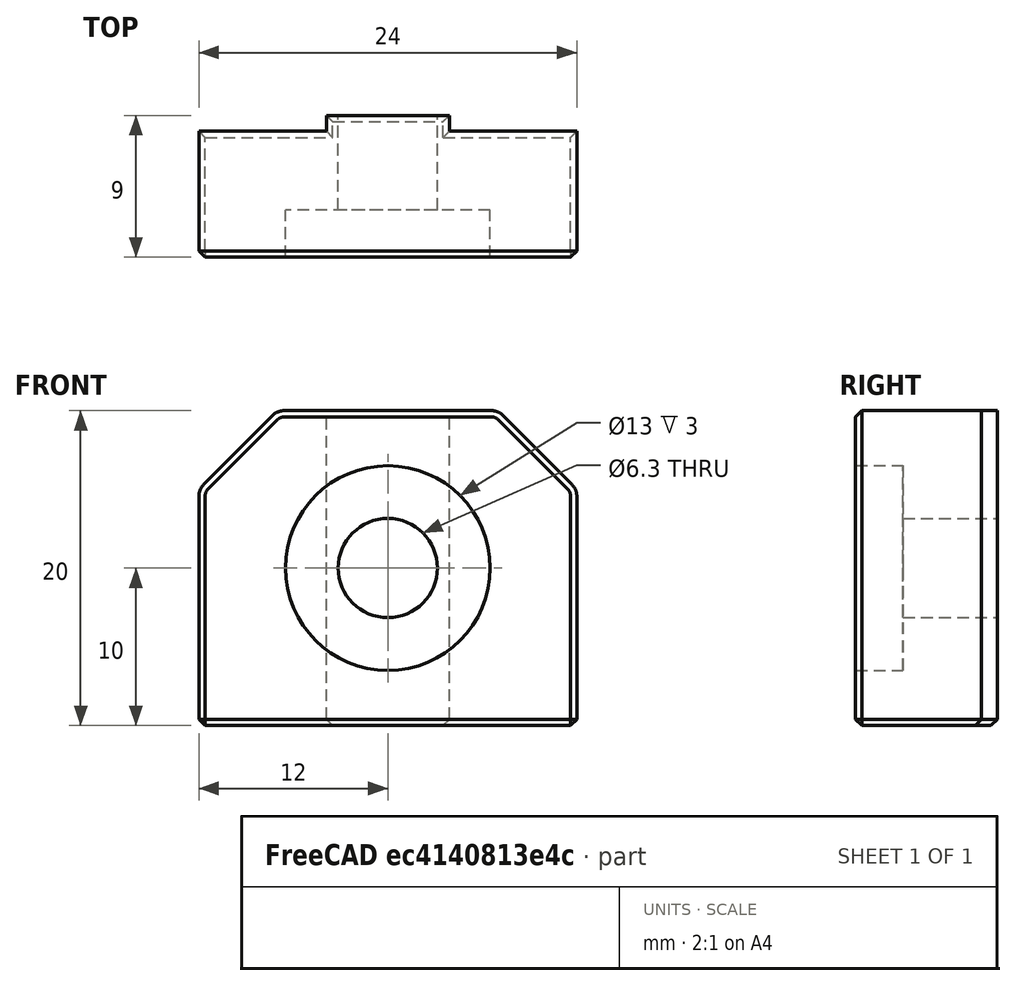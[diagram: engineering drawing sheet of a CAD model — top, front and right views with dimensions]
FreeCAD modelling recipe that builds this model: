
FCSTD DOCUMENT  (FreeCAD 0.19R24291 (Git))
Label: z-rail-encap
License: Other
LicenseURL: GPL3
objects: Part::Box×2, Part::Chamfer×2, Part::Cylinder×2, Part::MultiFuse×2, Part::Cut×1, Part::Fillet×1, Part::Refine×1
note: 11 computed .brp shape members not serialized (recipe doc carries the construction recipe); baked Part::Feature solids carry a one-line shape summary decoded from their .brp

FEATURE [Part::Box] Box  label="Cube"
  AttacherType = Attacher::AttachEngine3D
  Height = 20
  Length = 24
  Placement = pos=(-12,0,0) rot=(0,0,1;0rad)
  Width = 8
FEATURE [Part::Chamfer] Chamfer
  Base = -> Box
  Edges = 2 edges r=5: [Edge2,Edge6]
FEATURE [Part::Cylinder] Cylinder
  Angle = 360
  AttacherType = Attacher::AttachEngine3D
  Height = 10
  Placement = pos=(0,2.2e-15,10) rot=(1,0,0;4.71239rad)
  Radius = 3.15
FEATURE [Part::Cylinder] Cylinder001
  Angle = 360
  AttacherType = Attacher::AttachEngine3D
  Height = 3
  Placement = pos=(0,2e-15,10) rot=(-1,0,0;1.5708rad)
  Radius = 6.5
FEATURE [Part::MultiFuse] Fusion
  Shapes = -> [Cylinder001,Cylinder]
FEATURE [Part::Box] Box001  label="Cube001"
  AttacherType = Attacher::AttachEngine3D
  Height = 20
  Length = 7.8
  Placement = pos=(-3.9,8,0) rot=(0,0,1;0rad)
  Width = 1
FEATURE [Part::MultiFuse] Fusion001
  Shapes = -> [Box001,Chamfer]
FEATURE [Part::Cut] Cut
  Base = -> Fusion001
  Tool = -> Fusion
FEATURE [Part::Fillet] Fillet
  Base = -> Cut
  Edges = 4 edges r=1: [Edge4,Edge18,Edge20,Edge22]
FEATURE [Part::Refine] Fillet001
  Source = -> Fillet
FEATURE [Part::Chamfer] Chamfer001
  Base = -> Fillet001
  Edges = 17 edges r=0.4: [Edge1,Edge2,Edge5,Edge6,Edge7,Edge8,Edge9,Edge10,Edge11,Edge12,Edge13,Edge19,Edge22,Edge35,Edge40,Edge42,Edge47]
